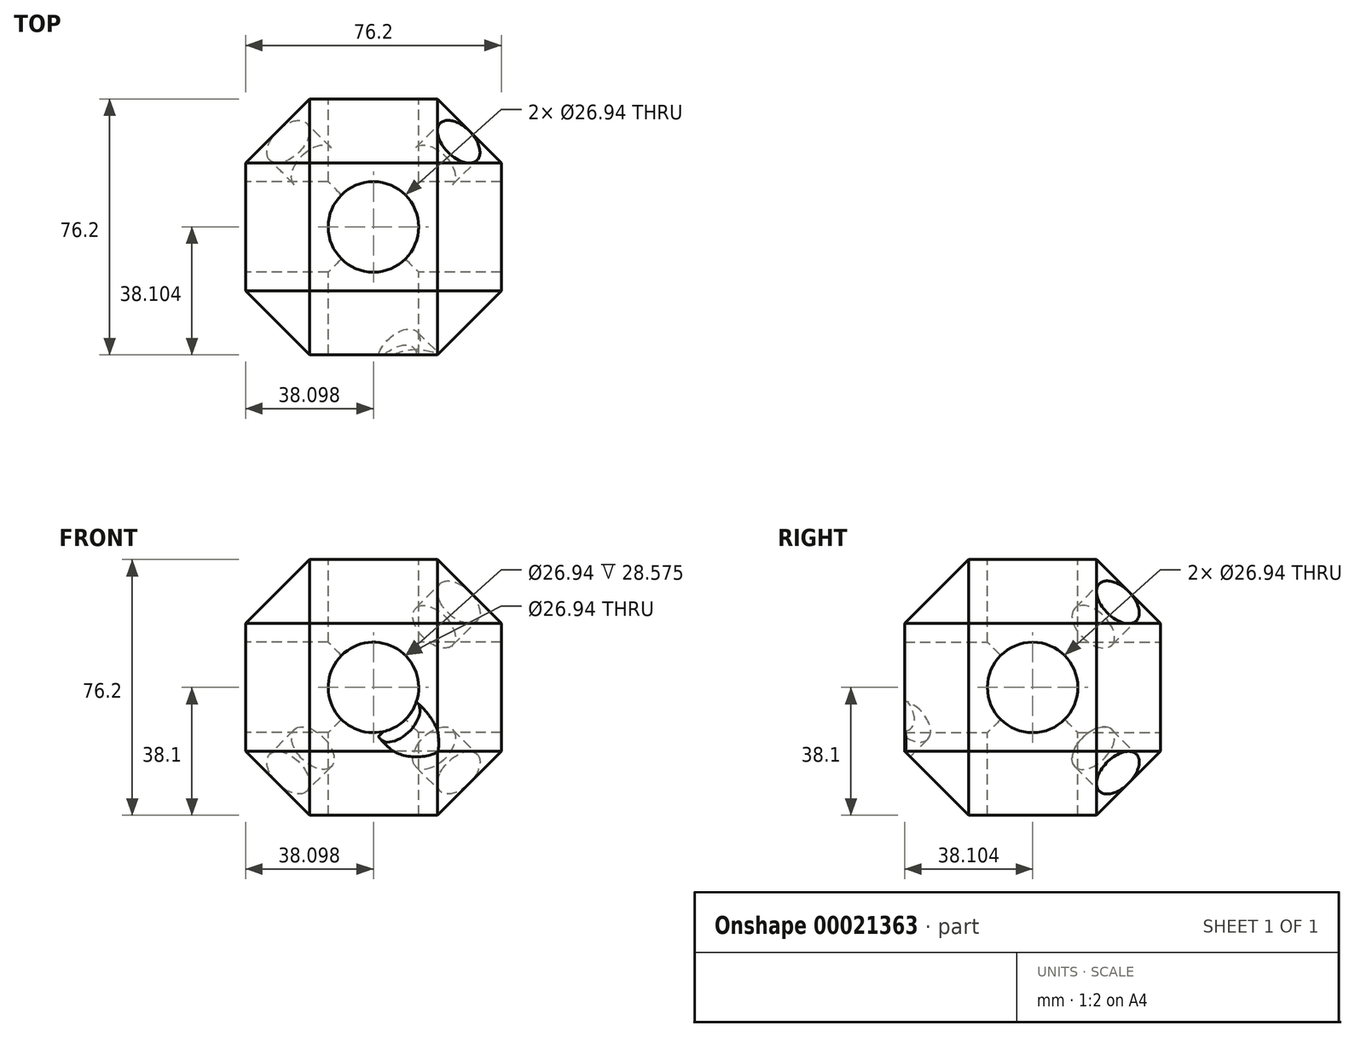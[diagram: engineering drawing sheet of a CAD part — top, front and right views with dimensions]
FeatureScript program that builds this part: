
annotation { "Feature Type Name" : "Feature", "Feature Type Description" : "" }
export const myFeature = defineFeature(function(context is Context, id is Id, definition is map)
    precondition{}
    {
        {
            var Q0;
            Q0=qCreatedBy(makeId("Top.planeOp"),FACE);
            var sketch = newSketch(context, id + "F0", { "sketchPlane" : qUnion([Q0])});
            skLineSegment(sketch, "E0.rect.bottom", {"start": v(29.23, 73.8) * mm, "end": v(-46.97, 73.8) * mm});
            skLineSegment(sketch, "E0.rect.top", {"start": v(29.23, -2.4) * mm, "end": v(-46.97, -2.4) * mm});
            skLineSegment(sketch, "E0.rect.left", {"start": v(29.23, 73.8) * mm, "end": v(29.23, -2.4) * mm});
            skLineSegment(sketch, "E0.rect.right", {"start": v(-46.97, 73.8) * mm, "end": v(-46.97, -2.4) * mm});
            skPoint(sketch, "E0.rect.middle", {"position": v(-8.87, 35.7) * mm});
            skSolve(sketch);
        }
        {
            var Q0;
            Q0 = qSketchRegion(id + "F0", true);
            extrude(context, id + "F1", {"entities" : qUnion([Q0]), "depth" : 76.2 * mm});
        }
        {
            var Q0;
            Q0=makeQuery(id+"F1.opExtrude","SWEPT_FACE",FACE,{"disambiguationData":[OSD([sQuery(id+"F0.wireOp",EDGE,"E0.rect.right")])]});
            var Q1;
            Q1=makeQuery(id+"F1.opExtrude","SWEPT_FACE",FACE,{"disambiguationData":[OSD([sQuery(id+"F0.wireOp",EDGE,"E0.rect.bottom")])]});
            var Q2;
            Q2=makeQuery(id+"F1.opExtrude","SWEPT_FACE",FACE,{"disambiguationData":[OSD([sQuery(id+"F0.wireOp",EDGE,"E0.rect.top")])]});
            var Q3;
            Q3=makeQuery(id+"F1.opExtrude","CAP_FACE",FACE,{"disambiguationData":[OSD([sQuery(id+"F0.wireOp",EDGE,"E0.rect.bottom"),sQuery(id+"F0.wireOp",EDGE,"E0.rect.top"),sQuery(id+"F0.wireOp",EDGE,"E0.rect.left"),sQuery(id+"F0.wireOp",EDGE,"E0.rect.right")])],"isStart":true});
            var Q4;
            Q4=makeQuery(id+"F1.opExtrude","SWEPT_FACE",FACE,{"disambiguationData":[OSD([sQuery(id+"F0.wireOp",EDGE,"E0.rect.left")])]});
            chamfer(context, id + "F2", {"entities" : qUnion([Q0, Q1, Q2, Q3, Q4]), "width" : 19.05 * mm, "tangentPropagation" : true});
        }
        {
            var Q0;
            Q0=makeQuery(id+"F1.opExtrude","CAP_FACE",FACE,{"disambiguationData":[OSD([sQuery(id+"F0.wireOp",EDGE,"E0.rect.bottom"),sQuery(id+"F0.wireOp",EDGE,"E0.rect.top"),sQuery(id+"F0.wireOp",EDGE,"E0.rect.left"),sQuery(id+"F0.wireOp",EDGE,"E0.rect.right")])],"isStart":false});
            var sketch = newSketch(context, id + "F3", { "sketchPlane" : qUnion([Q0])});
            skCircle(sketch, "E1", {"center": v(-8.87, 35.7) * mm, "radius": 13.47 * mm});
            skPoint(sketch, "E1.first.point", {"position": v(-18.4, 45.22) * mm});
            skPoint(sketch, "E1.second.point", {"position": v(0.65, 45.22) * mm});
            skPoint(sketch, "E1.third.point", {"position": v(0.65, 26.17) * mm});
            skSolve(sketch);
        }
        {
            var Q0;
            Q0 = qSketchRegion(id + "F3", true);
            extrude(context, id + "F4", {"entities" : qUnion([Q0]), "operationType" : NewBodyOperationType.REMOVE, "oppositeDirection" : true, "depth" : 127 * mm});
        }
        {
            var Q0;
            Q0=makeQuery(id+"F1.opExtrude","SWEPT_FACE",FACE,{"disambiguationData":[OSD([sQuery(id+"F0.wireOp",EDGE,"E0.rect.right")])]});
            var sketch = newSketch(context, id + "F5", { "sketchPlane" : qUnion([Q0])});
            skCircle(sketch, "E2", {"center": v(-35.7, 38.1) * mm, "radius": 13.47 * mm});
            skSolve(sketch);
        }
        {
            var Q0;
            Q0 = qSketchRegion(id + "F5", true);
            var Q1;
            Q1=makeQuery(id+"F5.imprint","IMPRINT",FACE,{"disambiguationData":[TD([[makeQuery(id+"F5.imprint","IMPRINT",EDGE,{"derivedFrom":sQuery(id+"F5.wireOp",EDGE,"E2")}),1.0]])]});
            extrude(context, id + "F6", {"entities" : qUnion([Q0, Q1]), "operationType" : NewBodyOperationType.REMOVE, "oppositeDirection" : true, "depth" : 127 * mm});
        }
        {
            var Q0;
            Q0=makeQuery(id+"F1.opExtrude","SWEPT_FACE",FACE,{"disambiguationData":[OSD([sQuery(id+"F0.wireOp",EDGE,"E0.rect.bottom")])]});
            var sketch = newSketch(context, id + "F7", { "sketchPlane" : qUnion([Q0])});
            skCircle(sketch, "E3", {"center": v(8.87, 38.1) * mm, "radius": 13.47 * mm});
            skSolve(sketch);
        }
        {
            var Q0;
            Q0 = qSketchRegion(id + "F7", true);
            extrude(context, id + "F8", {"entities" : qUnion([Q0]), "operationType" : NewBodyOperationType.REMOVE, "oppositeDirection" : true, "depth" : 127 * mm});
        }
        {
            var Q0;
            {var subQ0=sQuery(id+"F0.wireOp",EDGE,"E0.rect.bottom");var subQ1=sQuery(id+"F0.wireOp",EDGE,"E0.rect.left");Q0=makeQuery(id+"F2.opChamfer","BLEND_FACE",FACE,{"disambiguationData":[OSD([subQ0,subQ1]),TDD([makeQuery(id+"F1.opExtrude","CAP_VERTEX",VERTEX,{"disambiguationData":[OSD([subQ0,subQ1])],"isStart":true})])]});}
            var sketch = newSketch(context, id + "F9", { "sketchPlane" : qUnion([Q0])});
            skCircle(sketch, "E4", {"center": v(6.26, 52.18) * mm, "radius": 7.78 * mm});
            skPoint(sketch, "E4.first.point", {"position": v(2.37, 58.92) * mm});
            skPoint(sketch, "E4.second.point", {"position": v(14.04, 52.18) * mm});
            skPoint(sketch, "E4.third.point", {"position": v(2.37, 45.44) * mm});
            skSolve(sketch);
        }
        {
            var Q0;
            Q0 = qSketchRegion(id + "F9", true);
            extrude(context, id + "F10", {"entities" : qUnion([Q0]), "operationType" : NewBodyOperationType.REMOVE, "oppositeDirection" : true, "depth" : 12.7 * mm});
        }
        {
            var Q0;
            {var subQ0=sQuery(id+"F0.wireOp",EDGE,"E0.rect.bottom");var subQ1=sQuery(id+"F0.wireOp",EDGE,"E0.rect.left");Q0=makeQuery(id+"F2.opChamfer","BLEND_FACE",FACE,{"disambiguationData":[OSD([subQ0,subQ1]),TDD([makeQuery(id+"F1.opExtrude","CAP_VERTEX",VERTEX,{"disambiguationData":[OSD([subQ0,subQ1])],"isStart":false})])]});}
            var sketch = newSketch(context, id + "F11", { "sketchPlane" : qUnion([Q0])});
            skCircle(sketch, "E5", {"center": v(37.37, 1.7) * mm, "radius": 7.78 * mm});
            skPoint(sketch, "E5.first.point", {"position": v(45.15, 1.7) * mm});
            skPoint(sketch, "E5.second.point", {"position": v(33.48, 8.44) * mm});
            skPoint(sketch, "E5.third.point", {"position": v(33.48, -5.03) * mm});
            skSolve(sketch);
        }
        {
            var Q0;
            {var subQ0=sQuery(id+"F11.wireOp",EDGE,"E5");var subQ1=sQuery(id+"F0.wireOp",EDGE,"E0.rect.bottom");var subQ2=sQuery(id+"F0.wireOp",EDGE,"E0.rect.left");var subQ3=makeQuery(id+"F1.opExtrude","CAP_VERTEX",VERTEX,{"disambiguationData":[OSD([subQ1,subQ2])],"isStart":false});var subQ6=makeQuery(id+"F11.imprint","INTERSECT",VERTEX,{"derivedFrom":[makeQuery(id+"F2.opChamfer","BLEND_EDGE",EDGE,{"blendedFrom":[subQ3,makeQuery(id+"F1.opExtrude","CAP_EDGE",EDGE,{"disambiguationData":[OSD([subQ2])],"isStart":false})],"blendedInto":[]}),subQ0]});Q0=makeQuery(id+"F11.imprint","IMPRINT",FACE,{"disambiguationData":[TD([[makeQuery(id+"F11.imprint","IMPRINT",EDGE,{"disambiguationData":[TD([[subQ6,1.0]])],"derivedFrom":subQ0}),1.0]])]});}
            extrude(context, id + "F12", {"entities" : qUnion([Q0]), "operationType" : NewBodyOperationType.REMOVE, "oppositeDirection" : true, "depth" : 12.7 * mm});
        }
        {
            var Q0;
            {var subQ0=sQuery(id+"F0.wireOp",EDGE,"E0.rect.bottom");var subQ1=sQuery(id+"F0.wireOp",EDGE,"E0.rect.right");Q0=makeQuery(id+"F2.opChamfer","BLEND_FACE",FACE,{"disambiguationData":[OSD([subQ0,subQ1]),TDD([makeQuery(id+"F1.opExtrude","CAP_VERTEX",VERTEX,{"disambiguationData":[OSD([subQ0,subQ1])],"isStart":false})])]});}
            var sketch = newSketch(context, id + "F13", { "sketchPlane" : qUnion([Q0])});
            skCircle(sketch, "E6", {"center": v(22.88, -1.7) * mm, "radius": 7.78 * mm});
            skPoint(sketch, "E6.first.point", {"position": v(19, -8.44) * mm});
            skPoint(sketch, "E6.second.point", {"position": v(19, 5.03) * mm});
            skPoint(sketch, "E6.third.point", {"position": v(30.66, -1.7) * mm});
            skSolve(sketch);
        }
        {
            var Q0;
            Q0 = qSketchRegion(id + "F13", true);
            extrude(context, id + "F14", {"entities" : qUnion([Q0]), "operationType" : NewBodyOperationType.REMOVE, "oppositeDirection" : true, "depth" : 12.7 * mm});
        }
        {
            var Q0;
            {var subQ0=sQuery(id+"F0.wireOp",EDGE,"E0.rect.top");var subQ1=sQuery(id+"F0.wireOp",EDGE,"E0.rect.left");Q0=makeQuery(id+"F2.opChamfer","BLEND_FACE",FACE,{"disambiguationData":[OSD([subQ0,subQ1]),TDD([makeQuery(id+"F1.opExtrude","CAP_VERTEX",VERTEX,{"disambiguationData":[OSD([subQ0,subQ1])],"isStart":false})])]});}
            var sketch = newSketch(context, id + "F15", { "sketchPlane" : qUnion([Q0])});
            skCircle(sketch, "E7", {"center": v(41.08, 33.21) * mm, "radius": 7.78 * mm});
            skPoint(sketch, "E7.first.point", {"position": v(37.19, 39.95) * mm});
            skPoint(sketch, "E7.second.point", {"position": v(48.85, 33.21) * mm});
            skPoint(sketch, "E7.third.point", {"position": v(37.19, 26.48) * mm});
            skSolve(sketch);
        }
        {
            var Q0;
            {var subQ0=sQuery(id+"F15.wireOp",EDGE,"E7");var subQ1=sQuery(id+"F0.wireOp",EDGE,"E0.rect.top");var subQ2=sQuery(id+"F0.wireOp",EDGE,"E0.rect.left");var subQ3=makeQuery(id+"F1.opExtrude","CAP_VERTEX",VERTEX,{"disambiguationData":[OSD([subQ1,subQ2])],"isStart":false});var subQ6=makeQuery(id+"F15.imprint","INTERSECT",VERTEX,{"derivedFrom":[makeQuery(id+"F2.opChamfer","BLEND_EDGE",EDGE,{"blendedFrom":[subQ3,makeQuery(id+"F1.opExtrude","CAP_EDGE",EDGE,{"disambiguationData":[OSD([subQ1])],"isStart":false})],"blendedInto":[]}),subQ0]});Q0=makeQuery(id+"F15.imprint","IMPRINT",FACE,{"disambiguationData":[TD([[makeQuery(id+"F15.imprint","IMPRINT",EDGE,{"disambiguationData":[TD([[subQ6,1.0]])],"derivedFrom":subQ0}),1.0]])]});}
            extrude(context, id + "F16", {"entities" : qUnion([Q0]), "operationType" : NewBodyOperationType.REMOVE, "oppositeDirection" : true, "depth" : 12.7 * mm});
        }
        {
            var Q0;
            {var subQ0=sQuery(id+"F0.wireOp",EDGE,"E0.rect.top");var subQ1=sQuery(id+"F0.wireOp",EDGE,"E0.rect.left");Q0=makeQuery(id+"F2.opChamfer","BLEND_FACE",FACE,{"disambiguationData":[OSD([subQ0,subQ1]),TDD([makeQuery(id+"F1.opExtrude","CAP_VERTEX",VERTEX,{"disambiguationData":[OSD([subQ0,subQ1])],"isStart":true})])]});}
            var sketch = newSketch(context, id + "F17", { "sketchPlane" : qUnion([Q0])});
            skCircle(sketch, "E8", {"center": v(9.97, 20.67) * mm, "radius": 7.78 * mm});
            skPoint(sketch, "E8.first.point", {"position": v(17.74, 20.67) * mm});
            skPoint(sketch, "E8.second.point", {"position": v(6.08, 13.93) * mm});
            skPoint(sketch, "E8.third.point", {"position": v(6.08, 27.4) * mm});
            skSolve(sketch);
        }
        {
            var Q0;
            {var subQ0=sQuery(id+"F17.wireOp",EDGE,"E8");var subQ1=sQuery(id+"F0.wireOp",EDGE,"E0.rect.top");var subQ2=sQuery(id+"F0.wireOp",EDGE,"E0.rect.left");var subQ3=makeQuery(id+"F1.opExtrude","CAP_VERTEX",VERTEX,{"disambiguationData":[OSD([subQ1,subQ2])],"isStart":true});var subQ5=makeQuery(id+"F17.imprint","INTERSECT",VERTEX,{"derivedFrom":[makeQuery(id+"F2.opChamfer","BLEND_EDGE",EDGE,{"blendedFrom":[subQ3,makeQuery(id+"F1.opExtrude","CAP_EDGE",EDGE,{"disambiguationData":[OSD([subQ2])],"isStart":true})],"blendedInto":[]}),subQ0]});Q0=makeQuery(id+"F17.imprint","IMPRINT",FACE,{"disambiguationData":[TD([[makeQuery(id+"F17.imprint","IMPRINT",EDGE,{"disambiguationData":[TD([[subQ5,1.0]])],"derivedFrom":subQ0}),1.0]])]});}
            extrude(context, id + "F18", {"entities" : qUnion([Q0]), "operationType" : NewBodyOperationType.REMOVE, "oppositeDirection" : true, "depth" : 12.7 * mm});
        }
        {
            var Q0;
            {var subQ0=sQuery(id+"F0.wireOp",EDGE,"E0.rect.top");var subQ1=sQuery(id+"F0.wireOp",EDGE,"E0.rect.right");Q0=makeQuery(id+"F2.opChamfer","BLEND_FACE",FACE,{"disambiguationData":[OSD([subQ0,subQ1]),TDD([makeQuery(id+"F1.opExtrude","CAP_VERTEX",VERTEX,{"disambiguationData":[OSD([subQ0,subQ1])],"isStart":true})])]});}
            var sketch = newSketch(context, id + "F19", { "sketchPlane" : qUnion([Q0])});
            skCircle(sketch, "E9", {"center": v(-17.21, 33.21) * mm, "radius": 7.78 * mm});
            skPoint(sketch, "E9.first.point", {"position": v(-13.32, 26.48) * mm});
            skPoint(sketch, "E9.second.point", {"position": v(-24.99, 33.21) * mm});
            skPoint(sketch, "E9.third.point", {"position": v(-13.32, 39.95) * mm});
            skSolve(sketch);
        }
        {
            var Q0;
            {var subQ0=sQuery(id+"F19.wireOp",EDGE,"E9");var subQ1=sQuery(id+"F0.wireOp",EDGE,"E0.rect.top");var subQ2=sQuery(id+"F0.wireOp",EDGE,"E0.rect.right");var subQ3=makeQuery(id+"F1.opExtrude","CAP_VERTEX",VERTEX,{"disambiguationData":[OSD([subQ1,subQ2])],"isStart":true});var subQ6=makeQuery(id+"F19.imprint","INTERSECT",VERTEX,{"derivedFrom":[makeQuery(id+"F2.opChamfer","BLEND_EDGE",EDGE,{"blendedFrom":[subQ3,makeQuery(id+"F1.opExtrude","CAP_EDGE",EDGE,{"disambiguationData":[OSD([subQ2])],"isStart":true})],"blendedInto":[]}),subQ0]});Q0=makeQuery(id+"F19.imprint","IMPRINT",FACE,{"disambiguationData":[TD([[makeQuery(id+"F19.imprint","IMPRINT",EDGE,{"disambiguationData":[TD([[subQ6,-1.0]])],"derivedFrom":subQ0}),1.0]])]});}
            extrude(context, id + "F20", {"entities" : qUnion([Q0]), "operationType" : NewBodyOperationType.REMOVE, "oppositeDirection" : true, "depth" : 12.7 * mm});
        }
        {
            var Q0;
            {var subQ0=sQuery(id+"F0.wireOp",EDGE,"E0.rect.top");var subQ1=sQuery(id+"F0.wireOp",EDGE,"E0.rect.right");Q0=makeQuery(id+"F2.opChamfer","BLEND_FACE",FACE,{"disambiguationData":[OSD([subQ0,subQ1]),TDD([makeQuery(id+"F1.opExtrude","CAP_VERTEX",VERTEX,{"disambiguationData":[OSD([subQ0,subQ1])],"isStart":false})])]});}
            var sketch = newSketch(context, id + "F21", { "sketchPlane" : qUnion([Q0])});
            skCircle(sketch, "E10", {"center": v(-48.32, 20.67) * mm, "radius": 7.78 * mm});
            skPoint(sketch, "E10.first.point", {"position": v(-44.43, 13.93) * mm});
            skPoint(sketch, "E10.second.point", {"position": v(-44.43, 27.4) * mm});
            skPoint(sketch, "E10.third.point", {"position": v(-56.1, 20.67) * mm});
            skSolve(sketch);
        }
        {
            var Q0;
            {var subQ0=sQuery(id+"F21.wireOp",EDGE,"E10");var subQ1=sQuery(id+"F0.wireOp",EDGE,"E0.rect.top");var subQ2=sQuery(id+"F0.wireOp",EDGE,"E0.rect.right");var subQ3=makeQuery(id+"F1.opExtrude","CAP_VERTEX",VERTEX,{"disambiguationData":[OSD([subQ1,subQ2])],"isStart":false});var subQ6=makeQuery(id+"F21.imprint","INTERSECT",VERTEX,{"derivedFrom":[makeQuery(id+"F2.opChamfer","BLEND_EDGE",EDGE,{"blendedFrom":[subQ3,makeQuery(id+"F1.opExtrude","CAP_EDGE",EDGE,{"disambiguationData":[OSD([subQ2])],"isStart":false})],"blendedInto":[]}),subQ0]});Q0=makeQuery(id+"F21.imprint","IMPRINT",FACE,{"disambiguationData":[TD([[makeQuery(id+"F21.imprint","IMPRINT",EDGE,{"disambiguationData":[TD([[subQ6,1.0]])],"derivedFrom":subQ0}),1.0]])]});}
            extrude(context, id + "F22", {"entities" : qUnion([Q0]), "operationType" : NewBodyOperationType.REMOVE, "oppositeDirection" : true, "depth" : 12.7 * mm});
        }
        {
            var Q0;
            {var subQ0=sQuery(id+"F0.wireOp",EDGE,"E0.rect.bottom");var subQ1=sQuery(id+"F0.wireOp",EDGE,"E0.rect.right");Q0=makeQuery(id+"F2.opChamfer","BLEND_FACE",FACE,{"disambiguationData":[OSD([subQ0,subQ1]),TDD([makeQuery(id+"F1.opExtrude","CAP_VERTEX",VERTEX,{"disambiguationData":[OSD([subQ0,subQ1])],"isStart":true})])]});}
            var sketch = newSketch(context, id + "F23", { "sketchPlane" : qUnion([Q0])});
            skCircle(sketch, "E11", {"center": v(8.23, 52.18) * mm, "radius": 7.78 * mm});
            skPoint(sketch, "E11.first.point", {"position": v(12.11, 45.44) * mm});
            skPoint(sketch, "E11.second.point", {"position": v(0.45, 52.18) * mm});
            skPoint(sketch, "E11.third.point", {"position": v(12.11, 58.92) * mm});
            skSolve(sketch);
        }
        {
            var Q0;
            {var subQ0=sQuery(id+"F23.wireOp",EDGE,"E11");var subQ1=sQuery(id+"F0.wireOp",EDGE,"E0.rect.bottom");var subQ2=sQuery(id+"F0.wireOp",EDGE,"E0.rect.right");var subQ3=makeQuery(id+"F1.opExtrude","CAP_VERTEX",VERTEX,{"disambiguationData":[OSD([subQ1,subQ2])],"isStart":true});var subQ6=makeQuery(id+"F23.imprint","INTERSECT",VERTEX,{"derivedFrom":[makeQuery(id+"F2.opChamfer","BLEND_EDGE",EDGE,{"blendedFrom":[subQ3,makeQuery(id+"F1.opExtrude","CAP_EDGE",EDGE,{"disambiguationData":[OSD([subQ1])],"isStart":true})],"blendedInto":[]}),subQ0]});Q0=makeQuery(id+"F23.imprint","IMPRINT",FACE,{"disambiguationData":[TD([[makeQuery(id+"F23.imprint","IMPRINT",EDGE,{"disambiguationData":[TD([[subQ6,-1.0]])],"derivedFrom":subQ0}),1.0]])]});}
            extrude(context, id + "F24", {"entities" : qUnion([Q0]), "operationType" : NewBodyOperationType.REMOVE, "oppositeDirection" : true, "depth" : 12.7 * mm});
        }
    });
